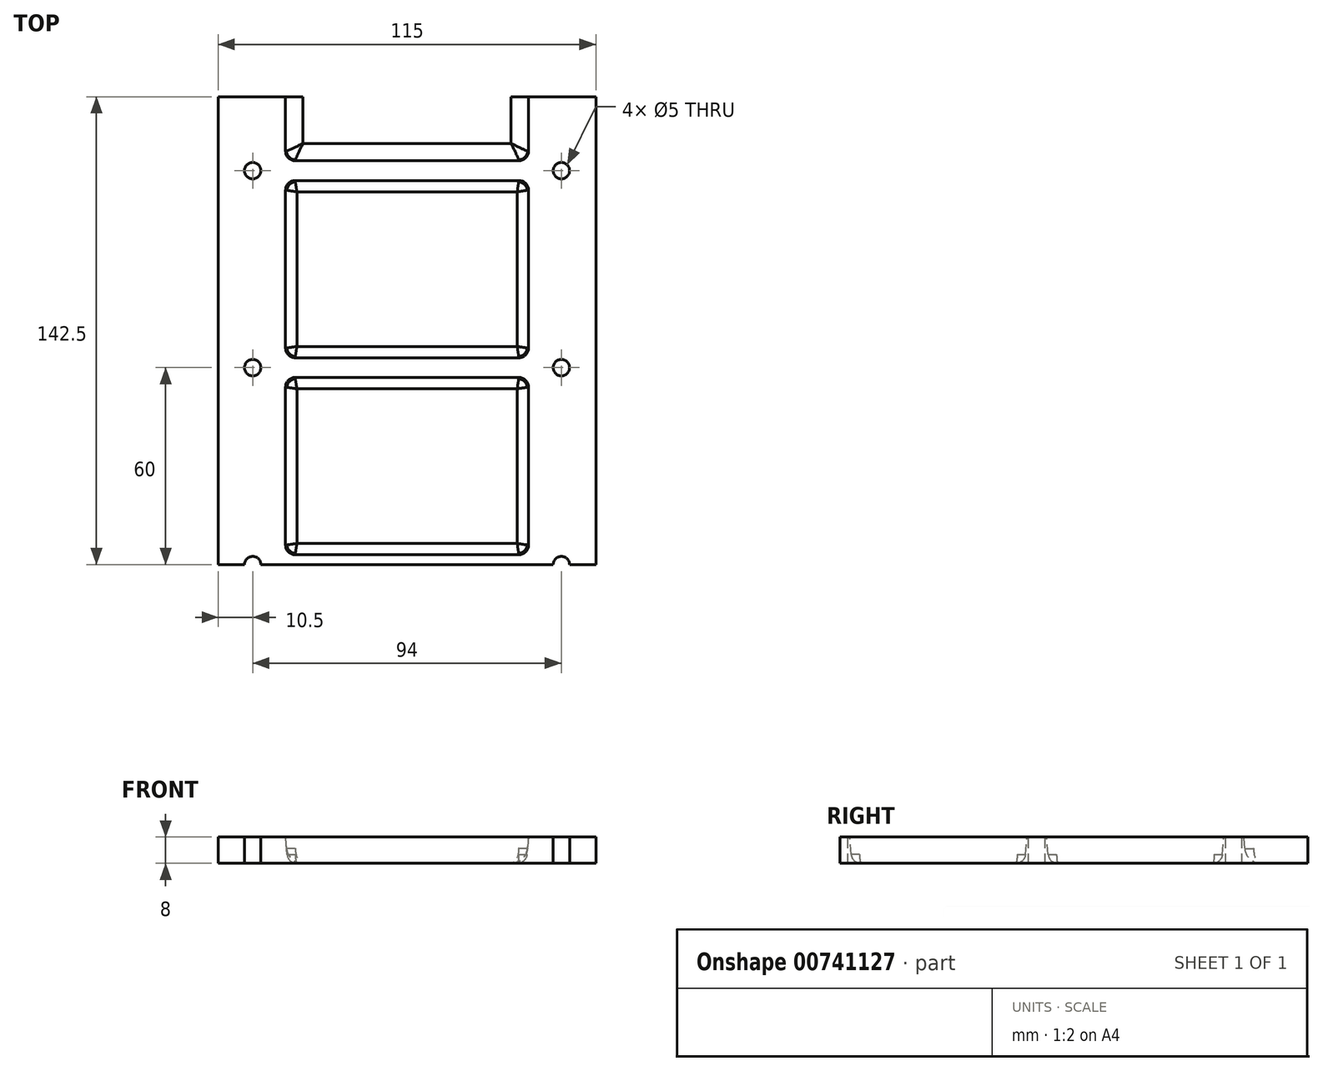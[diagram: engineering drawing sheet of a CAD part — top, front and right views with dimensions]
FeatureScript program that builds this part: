
annotation { "Feature Type Name" : "Feature", "Feature Type Description" : "" }
export const myFeature = defineFeature(function(context is Context, id is Id, definition is map)
    precondition{}
    {
        {
            var Q0;
            Q0=qCreatedBy(makeId("Top.planeOp"),FACE);
            var sketch = newSketch(context, id + "F0", { "sketchPlane" : qUnion([Q0])});
            skLineSegment(sketch, "E0.bottom", {"start": v(-57.5, -142.5) * mm, "end": v(57.5, -142.5) * mm});
            skLineSegment(sketch, "E0.top", {"start": v(-57.5, 142.5) * mm, "end": v(57.5, 142.5) * mm});
            skLineSegment(sketch, "E0.left", {"start": v(-57.5, -142.5) * mm, "end": v(-57.5, 142.5) * mm});
            skLineSegment(sketch, "E0.right", {"start": v(57.5, -142.5) * mm, "end": v(57.5, 142.5) * mm});
            skCircle(sketch, "E1", {"center": v(47, 0) * mm, "radius": 2.5 * mm});
            skCircle(sketch, "E2.0.1.0", {"center": v(47, 60) * mm, "radius": 2.5 * mm});
            skCircle(sketch, "E2.0.2.0", {"center": v(47, 120) * mm, "radius": 2.5 * mm});
            skCircle(sketch, "E2.1.0.0", {"center": v(-47, 0) * mm, "radius": 2.5 * mm});
            skCircle(sketch, "E2.1.1.0", {"center": v(-47, 60) * mm, "radius": 2.5 * mm});
            skCircle(sketch, "E2.1.2.0", {"center": v(-47, 120) * mm, "radius": 2.5 * mm});
            skLineSegment(sketch, "E2.direction1", {"start": v(47, 0) * mm, "end": v(-47, 0) * mm, "construction": true});
            skCircle(sketch, "E3.0.1.0", {"center": v(47, -60) * mm, "radius": 2.5 * mm});
            skCircle(sketch, "E3.0.2.0", {"center": v(47, -120) * mm, "radius": 2.5 * mm});
            skCircle(sketch, "E3.1.1.0", {"center": v(-47, -60) * mm, "radius": 2.5 * mm});
            skLineSegment(sketch, "E3.direction2", {"start": v(47, 0) * mm, "end": v(47, -60) * mm, "construction": true});
            skSolve(sketch);
        }
        {
            var Q0;
            Q0 = qSketchRegion(id + "F0", true);
            extrude(context, id + "F1", {"entities" : qUnion([Q0]), "depth" : 10 * mm, "offsetDistance" : 25 * mm});
        }
        {
            var Q0;
            Q0=qCreatedBy(makeId("Top.planeOp"),FACE);
            var sketch = newSketch(context, id + "F2", { "sketchPlane" : qUnion([Q0])});
            skLineSegment(sketch, "E4.bottom", {"start": v(-34, 3) * mm, "end": v(34, 3) * mm});
            skLineSegment(sketch, "E4.top", {"start": v(-34, 57) * mm, "end": v(34, 57) * mm});
            skLineSegment(sketch, "E4.left", {"start": v(-37, 6) * mm, "end": v(-37, 54) * mm});
            skLineSegment(sketch, "E4.right", {"start": v(37, 6) * mm, "end": v(37, 54) * mm});
            skPoint(sketch, "E5.visualSharp", {"position": v(-37, 57) * mm});
            skArc(sketch, "E5.filletArc", {"start": v(-34, 57) * mm, "mid": v(-36.12, 56.12) * mm, "end": v(-37, 54) * mm});
            skPoint(sketch, "E6.visualSharp", {"position": v(37, 57) * mm});
            skArc(sketch, "E6.filletArc", {"start": v(37, 54) * mm, "mid": v(36.12, 56.12) * mm, "end": v(34, 57) * mm});
            skPoint(sketch, "E7.visualSharp", {"position": v(37, 3) * mm});
            skArc(sketch, "E7.filletArc", {"start": v(34, 3) * mm, "mid": v(36.12, 3.88) * mm, "end": v(37, 6) * mm});
            skPoint(sketch, "E8.visualSharp", {"position": v(-37, 3) * mm});
            skArc(sketch, "E8.filletArc", {"start": v(-37, 6) * mm, "mid": v(-36.12, 3.88) * mm, "end": v(-34, 3) * mm});
            skLineSegment(sketch, "E9.0.1.0", {"start": v(-34, 117) * mm, "end": v(34, 117) * mm});
            skLineSegment(sketch, "E9.0.1.1", {"start": v(-37, 66) * mm, "end": v(-37, 114) * mm});
            skPoint(sketch, "E9.0.1.2", {"position": v(-37, 117) * mm});
            skLineSegment(sketch, "E9.0.1.3", {"start": v(-34, 63) * mm, "end": v(34, 63) * mm});
            skPoint(sketch, "E9.0.1.4", {"position": v(-37, 63) * mm});
            skLineSegment(sketch, "E9.0.1.5", {"start": v(37, 66) * mm, "end": v(37, 114) * mm});
            skPoint(sketch, "E9.0.1.6", {"position": v(37, 63) * mm});
            skPoint(sketch, "E9.0.1.7", {"position": v(37, 117) * mm});
            skArc(sketch, "E9.0.1.8", {"start": v(-37, 66) * mm, "mid": v(-36.12, 63.88) * mm, "end": v(-34, 63) * mm});
            skArc(sketch, "E9.0.1.9", {"start": v(34, 63) * mm, "mid": v(36.12, 63.88) * mm, "end": v(37, 66) * mm});
            skArc(sketch, "E9.0.1.10", {"start": v(37, 114) * mm, "mid": v(36.12, 116.12) * mm, "end": v(34, 117) * mm});
            skArc(sketch, "E9.0.1.11", {"start": v(-34, 117) * mm, "mid": v(-36.12, 116.12) * mm, "end": v(-37, 114) * mm});
            skLineSegment(sketch, "E9.direction1", {"start": v(-37, 3) * mm, "end": v(-12, 3) * mm, "construction": true});
            skLineSegment(sketch, "E9.direction2", {"start": v(-37, 3) * mm, "end": v(-37, 63) * mm, "construction": true});
            skLineSegment(sketch, "E10.0.1.0", {"start": v(-37, -57) * mm, "end": v(-37, 3) * mm, "construction": true});
            skLineSegment(sketch, "E10.0.1.1", {"start": v(37, -54) * mm, "end": v(37, -6) * mm});
            skLineSegment(sketch, "E10.0.1.2", {"start": v(-34, -57) * mm, "end": v(34, -57) * mm});
            skLineSegment(sketch, "E10.0.1.3", {"start": v(-34, -3) * mm, "end": v(34, -3) * mm});
            skPoint(sketch, "E10.0.1.4", {"position": v(-37, -57) * mm});
            skPoint(sketch, "E10.0.1.7", {"position": v(37, -3) * mm});
            skPoint(sketch, "E10.0.1.8", {"position": v(37, -57) * mm});
            skPoint(sketch, "E10.0.1.9", {"position": v(-37, -3) * mm});
            skLineSegment(sketch, "E10.0.1.10", {"start": v(-37, -57) * mm, "end": v(-12, -57) * mm, "construction": true});
            skArc(sketch, "E10.0.1.11", {"start": v(34, -57) * mm, "mid": v(36.12, -56.12) * mm, "end": v(37, -54) * mm});
            skArc(sketch, "E10.0.1.12", {"start": v(37, -6) * mm, "mid": v(36.12, -3.88) * mm, "end": v(34, -3) * mm});
            skLineSegment(sketch, "E10.0.1.13", {"start": v(-37, -54) * mm, "end": v(-37, -6) * mm});
            skArc(sketch, "E10.0.1.14", {"start": v(-34, -3) * mm, "mid": v(-36.12, -3.88) * mm, "end": v(-37, -6) * mm});
            skArc(sketch, "E10.0.1.15", {"start": v(-37, -54) * mm, "mid": v(-36.12, -56.12) * mm, "end": v(-34, -57) * mm});
            skLineSegment(sketch, "E10.0.2.0", {"start": v(-37, -117) * mm, "end": v(-37, -57) * mm, "construction": true});
            skLineSegment(sketch, "E10.0.2.1", {"start": v(37, -114) * mm, "end": v(37, -66) * mm});
            skLineSegment(sketch, "E10.0.2.2", {"start": v(-34, -117) * mm, "end": v(34, -117) * mm});
            skLineSegment(sketch, "E10.0.2.3", {"start": v(-34, -63) * mm, "end": v(34, -63) * mm});
            skPoint(sketch, "E10.0.2.4", {"position": v(-37, -117) * mm});
            skPoint(sketch, "E10.0.2.5", {"position": v(37, -57) * mm});
            skPoint(sketch, "E10.0.2.6", {"position": v(-37, -57) * mm});
            skPoint(sketch, "E10.0.2.7", {"position": v(37, -63) * mm});
            skPoint(sketch, "E10.0.2.8", {"position": v(37, -117) * mm});
            skPoint(sketch, "E10.0.2.9", {"position": v(-37, -63) * mm});
            skLineSegment(sketch, "E10.0.2.10", {"start": v(-37, -117) * mm, "end": v(-12, -117) * mm, "construction": true});
            skArc(sketch, "E10.0.2.11", {"start": v(34, -117) * mm, "mid": v(36.12, -116.12) * mm, "end": v(37, -114) * mm});
            skArc(sketch, "E10.0.2.12", {"start": v(37, -66) * mm, "mid": v(36.12, -63.88) * mm, "end": v(34, -63) * mm});
            skLineSegment(sketch, "E10.0.2.13", {"start": v(-37, -114) * mm, "end": v(-37, -66) * mm});
            skArc(sketch, "E10.0.2.14", {"start": v(-34, -63) * mm, "mid": v(-36.12, -63.88) * mm, "end": v(-37, -66) * mm});
            skArc(sketch, "E10.0.2.15", {"start": v(-37, -114) * mm, "mid": v(-36.12, -116.12) * mm, "end": v(-34, -117) * mm});
            skLineSegment(sketch, "E10.direction2", {"start": v(-37, 3) * mm, "end": v(-37, -57) * mm, "construction": true});
            skLineSegment(sketch, "E11.0.0.3", {"start": v(-37, -177) * mm, "end": v(-37, -117) * mm, "construction": true});
            skLineSegment(sketch, "E11.3.0.3", {"start": v(37, -174) * mm, "end": v(37, -126) * mm});
            skLineSegment(sketch, "E11.6.0.3", {"start": v(-34, -177) * mm, "end": v(34, -177) * mm});
            skLineSegment(sketch, "E11.9.0.3", {"start": v(-34, -123) * mm, "end": v(34, -123) * mm});
            skPoint(sketch, "E11.12.0.3", {"position": v(-37, -177) * mm});
            skPoint(sketch, "E11.15.0.3", {"position": v(37, -123) * mm});
            skPoint(sketch, "E11.16.0.3", {"position": v(37, -177) * mm});
            skPoint(sketch, "E11.17.0.3", {"position": v(-37, -123) * mm});
            skLineSegment(sketch, "E11.18.0.3", {"start": v(-37, -177) * mm, "end": v(-12, -177) * mm, "construction": true});
            skArc(sketch, "E11.21.0.3", {"start": v(34, -177) * mm, "mid": v(36.12, -176.12) * mm, "end": v(37, -174) * mm});
            skArc(sketch, "E11.25.0.3", {"start": v(37, -126) * mm, "mid": v(36.12, -123.88) * mm, "end": v(34, -123) * mm});
            skLineSegment(sketch, "E11.29.0.3", {"start": v(-37, -174) * mm, "end": v(-37, -126) * mm});
            skArc(sketch, "E11.32.0.3", {"start": v(-34, -123) * mm, "mid": v(-36.12, -123.88) * mm, "end": v(-37, -126) * mm});
            skArc(sketch, "E11.36.0.3", {"start": v(-37, -174) * mm, "mid": v(-36.12, -176.12) * mm, "end": v(-34, -177) * mm});
            skLineSegment(sketch, "E12.0.0.2", {"start": v(-34, 177) * mm, "end": v(34, 177) * mm});
            skLineSegment(sketch, "E12.3.0.2", {"start": v(-37, 126) * mm, "end": v(-37, 174) * mm});
            skPoint(sketch, "E12.6.0.2", {"position": v(-37, 177) * mm});
            skLineSegment(sketch, "E12.7.0.2", {"start": v(-34, 123) * mm, "end": v(34, 123) * mm});
            skPoint(sketch, "E12.10.0.2", {"position": v(-37, 123) * mm});
            skLineSegment(sketch, "E12.11.0.2", {"start": v(37, 126) * mm, "end": v(37, 174) * mm});
            skPoint(sketch, "E12.14.0.2", {"position": v(37, 123) * mm});
            skPoint(sketch, "E12.15.0.2", {"position": v(37, 177) * mm});
            skArc(sketch, "E12.16.0.2", {"start": v(-37, 126) * mm, "mid": v(-36.12, 123.88) * mm, "end": v(-34, 123) * mm});
            skArc(sketch, "E12.20.0.2", {"start": v(34, 123) * mm, "mid": v(36.12, 123.88) * mm, "end": v(37, 126) * mm});
            skArc(sketch, "E12.24.0.2", {"start": v(37, 174) * mm, "mid": v(36.12, 176.12) * mm, "end": v(34, 177) * mm});
            skArc(sketch, "E12.28.0.2", {"start": v(-34, 177) * mm, "mid": v(-36.12, 176.12) * mm, "end": v(-37, 174) * mm});
            skSolve(sketch);
        }
        {
            var Q0;
            Q0 = qSketchRegion(id + "F2", true);
            extrude(context, id + "F3", {"entities" : qUnion([Q0]), "operationType" : NewBodyOperationType.REMOVE, "depth" : 8 * mm, "offsetDistance" : 25 * mm, "hasDraft" : true, "draftAngle" : 5 * degree, "draftPullDirection" : true});
        }
        {
            var Q0;
            Q0=makeQuery(id+"F3.boolean.opBoolean","COPY",FACE,{"derivedFrom":makeQuery(id+"F3.opExtrude","CAP_FACE",FACE,{"disambiguationData":[OSD([sQuery(id+"F2.wireOp",EDGE,"E10.0.2.1"),sQuery(id+"F2.wireOp",EDGE,"E10.0.2.2"),sQuery(id+"F2.wireOp",EDGE,"E10.0.2.3"),sQuery(id+"F2.wireOp",EDGE,"E10.0.2.11"),sQuery(id+"F2.wireOp",EDGE,"E10.0.2.12"),sQuery(id+"F2.wireOp",EDGE,"E10.0.2.13"),sQuery(id+"F2.wireOp",EDGE,"E10.0.2.14"),sQuery(id+"F2.wireOp",EDGE,"E10.0.2.15")])],"isStart":false})});
            var Q1;
            Q1=makeQuery(id+"F3.boolean.opBoolean","COPY",FACE,{"derivedFrom":makeQuery(id+"F3.opExtrude","CAP_FACE",FACE,{"disambiguationData":[OSD([sQuery(id+"F2.wireOp",EDGE,"E10.0.1.1"),sQuery(id+"F2.wireOp",EDGE,"E10.0.1.2"),sQuery(id+"F2.wireOp",EDGE,"E10.0.1.3"),sQuery(id+"F2.wireOp",EDGE,"E10.0.1.11"),sQuery(id+"F2.wireOp",EDGE,"E10.0.1.12"),sQuery(id+"F2.wireOp",EDGE,"E10.0.1.13"),sQuery(id+"F2.wireOp",EDGE,"E10.0.1.14"),sQuery(id+"F2.wireOp",EDGE,"E10.0.1.15")])],"isStart":false})});
            var Q2;
            Q2=makeQuery(id+"F3.boolean.opBoolean","COPY",FACE,{"derivedFrom":makeQuery(id+"F3.opExtrude","CAP_FACE",FACE,{"disambiguationData":[OSD([sQuery(id+"F2.wireOp",EDGE,"E4.bottom"),sQuery(id+"F2.wireOp",EDGE,"E4.top"),sQuery(id+"F2.wireOp",EDGE,"E4.left"),sQuery(id+"F2.wireOp",EDGE,"E4.right"),sQuery(id+"F2.wireOp",EDGE,"E5.filletArc"),sQuery(id+"F2.wireOp",EDGE,"E6.filletArc"),sQuery(id+"F2.wireOp",EDGE,"E7.filletArc"),sQuery(id+"F2.wireOp",EDGE,"E8.filletArc")])],"isStart":false})});
            var Q3;
            Q3=makeQuery(id+"F3.boolean.opBoolean","COPY",FACE,{"derivedFrom":makeQuery(id+"F3.opExtrude","CAP_FACE",FACE,{"disambiguationData":[OSD([sQuery(id+"F2.wireOp",EDGE,"E9.0.1.0"),sQuery(id+"F2.wireOp",EDGE,"E9.0.1.1"),sQuery(id+"F2.wireOp",EDGE,"E9.0.1.3"),sQuery(id+"F2.wireOp",EDGE,"E9.0.1.5"),sQuery(id+"F2.wireOp",EDGE,"E9.0.1.8"),sQuery(id+"F2.wireOp",EDGE,"E9.0.1.9"),sQuery(id+"F2.wireOp",EDGE,"E9.0.1.10"),sQuery(id+"F2.wireOp",EDGE,"E9.0.1.11")])],"isStart":false})});
            fillet(context, id + "F4", {"entities" : qUnion([Q0, Q1, Q2, Q3]), "radius" : 3 * mm, "tangentPropagation" : true, "allowEdgeOverflow" : false});
        }
        {
            var Q0;
            Q0=makeQuery(id+"F3.boolean.opBoolean","COPY",EDGE,{"derivedFrom":makeQuery(id+"F3.opExtrude","CAP_EDGE",EDGE,{"disambiguationData":[OSD([sQuery(id+"F2.wireOp",EDGE,"E11.3.0.3")])],"isStart":false})});
            var Q1;
            Q1=makeQuery(id+"F3.boolean.opBoolean","COPY",EDGE,{"derivedFrom":makeQuery(id+"F3.opExtrude","CAP_EDGE",EDGE,{"disambiguationData":[OSD([sQuery(id+"F2.wireOp",EDGE,"E11.25.0.3")])],"isStart":false})});
            fillet(context, id + "F5", {"entities" : qUnion([Q0, Q1]), "radius" : 5 * mm, "tangentPropagation" : true, "allowEdgeOverflow" : false});
        }
        {
            var Q0;
            Q0=makeQuery(id+"F3.boolean.opBoolean","COPY",EDGE,{"derivedFrom":makeQuery(id+"F3.opExtrude","CAP_EDGE",EDGE,{"disambiguationData":[OSD([sQuery(id+"F2.wireOp",EDGE,"E12.3.0.2")])],"isStart":false})});
            fillet(context, id + "F6", {"entities" : qUnion([Q0]), "radius" : 5 * mm, "tangentPropagation" : true, "allowEdgeOverflow" : false});
        }
        {
            var Q0;
            Q0=makeQuery(id+"F1.opExtrude","CAP_FACE",FACE,{"disambiguationData":[OSD([sQuery(id+"F0.wireOp",EDGE,"E0.bottom"),sQuery(id+"F0.wireOp",EDGE,"E0.top"),sQuery(id+"F0.wireOp",EDGE,"E0.left"),sQuery(id+"F0.wireOp",EDGE,"E0.right"),sQuery(id+"F0.wireOp",EDGE,"E1"),sQuery(id+"F0.wireOp",EDGE,"E2.0.1.0"),sQuery(id+"F0.wireOp",EDGE,"E2.0.2.0"),sQuery(id+"F0.wireOp",EDGE,"E2.1.1.0"),sQuery(id+"F0.wireOp",EDGE,"E2.1.2.0"),sQuery(id+"F0.wireOp",EDGE,"E3.0.1.0"),sQuery(id+"F0.wireOp",EDGE,"E3.0.2.0"),sQuery(id+"F0.wireOp",EDGE,"E2.1.0.0"),sQuery(id+"F0.wireOp",EDGE,"E3.1.1.0")])],"isStart":false});
            var sketch = newSketch(context, id + "F7", { "sketchPlane" : qUnion([Q0])});
            skLineSegment(sketch, "E13.bottom", {"start": v(-71.5, 160.57) * mm, "end": v(99.67, 160.57) * mm});
            skLineSegment(sketch, "E13.top", {"start": v(-71.5, -179.76) * mm, "end": v(99.67, -179.76) * mm});
            skLineSegment(sketch, "E13.left", {"start": v(-71.5, 160.57) * mm, "end": v(-71.5, -179.76) * mm});
            skLineSegment(sketch, "E13.right", {"start": v(99.67, 160.57) * mm, "end": v(99.67, -179.76) * mm});
            skSolve(sketch);
        }
        {
            var Q0;
            Q0 = qSketchRegion(id + "F7", true);
            extrude(context, id + "F8", {"entities" : qUnion([Q0]), "operationType" : NewBodyOperationType.REMOVE, "oppositeDirection" : true, "depth" : 2 * mm, "offsetDistance" : 25 * mm});
        }
        {
            var Q0;
            Q0=qCreatedBy(makeId("Top.planeOp"),FACE);
            var sketch = newSketch(context, id + "F9", { "sketchPlane" : qUnion([Q0])});
            skLineSegment(sketch, "E14.bottom", {"start": v(-69.34, 0) * mm, "end": v(65.21, 0) * mm});
            skLineSegment(sketch, "E14.top", {"start": v(-69.34, -146.3) * mm, "end": v(65.21, -146.3) * mm});
            skLineSegment(sketch, "E14.left", {"start": v(-69.34, 0) * mm, "end": v(-69.34, -146.3) * mm});
            skLineSegment(sketch, "E14.right", {"start": v(65.21, 0) * mm, "end": v(65.21, -146.3) * mm});
            skSolve(sketch);
        }
        {
            var Q0;
            Q0 = qSketchRegion(id + "F9", true);
            extrude(context, id + "F10", {"entities" : qUnion([Q0]), "operationType" : NewBodyOperationType.REMOVE, "depth" : 25 * mm, "offsetDistance" : 25 * mm});
        }
        {
            var Q0;
            Q0=makeQuery(id+"F1.opExtrude","SWEPT_BODY",BODY,{"disambiguationData":[OSD([sQuery(id+"F0.wireOp",EDGE,"E0.bottom"),sQuery(id+"F0.wireOp",EDGE,"E0.top"),sQuery(id+"F0.wireOp",EDGE,"E0.left"),sQuery(id+"F0.wireOp",EDGE,"E0.right"),sQuery(id+"F0.wireOp",EDGE,"E1"),sQuery(id+"F0.wireOp",EDGE,"E2.0.1.0"),sQuery(id+"F0.wireOp",EDGE,"E2.0.2.0"),sQuery(id+"F0.wireOp",EDGE,"E2.1.1.0"),sQuery(id+"F0.wireOp",EDGE,"E2.1.2.0"),sQuery(id+"F0.wireOp",EDGE,"E3.0.1.0"),sQuery(id+"F0.wireOp",EDGE,"E3.0.2.0"),sQuery(id+"F0.wireOp",EDGE,"E2.1.0.0"),sQuery(id+"F0.wireOp",EDGE,"E3.1.1.0")])]});
            var Q1;
            Q1=makeQuery(id+"F1.opExtrude","CAP_EDGE",EDGE,{"disambiguationData":[OSD([sQuery(id+"F0.wireOp",EDGE,"E0.right")])],"isStart":true});
            var Q2;
            Q2=makeQuery(id+"F1.opExtrude","CAP_VERTEX",VERTEX,{"disambiguationData":[OSD([sQuery(id+"F0.wireOp",EDGE,"E0.top"),sQuery(id+"F0.wireOp",EDGE,"E0.right")])],"isStart":true});
            var Q3;
            Q3=makeQuery(id+"F1.opExtrude","CAP_EDGE",EDGE,{"disambiguationData":[OSD([sQuery(id+"F0.wireOp",EDGE,"E0.right")])],"isStart":true});
            transform(context, id + "F11", {"entities" : qUnion([Q0]), "transformType" : TransformType.ROTATION, "transformAxis" : qUnion([Q3]), "angle" : 180 * degree, "makeCopy" : false});
        }
    });
